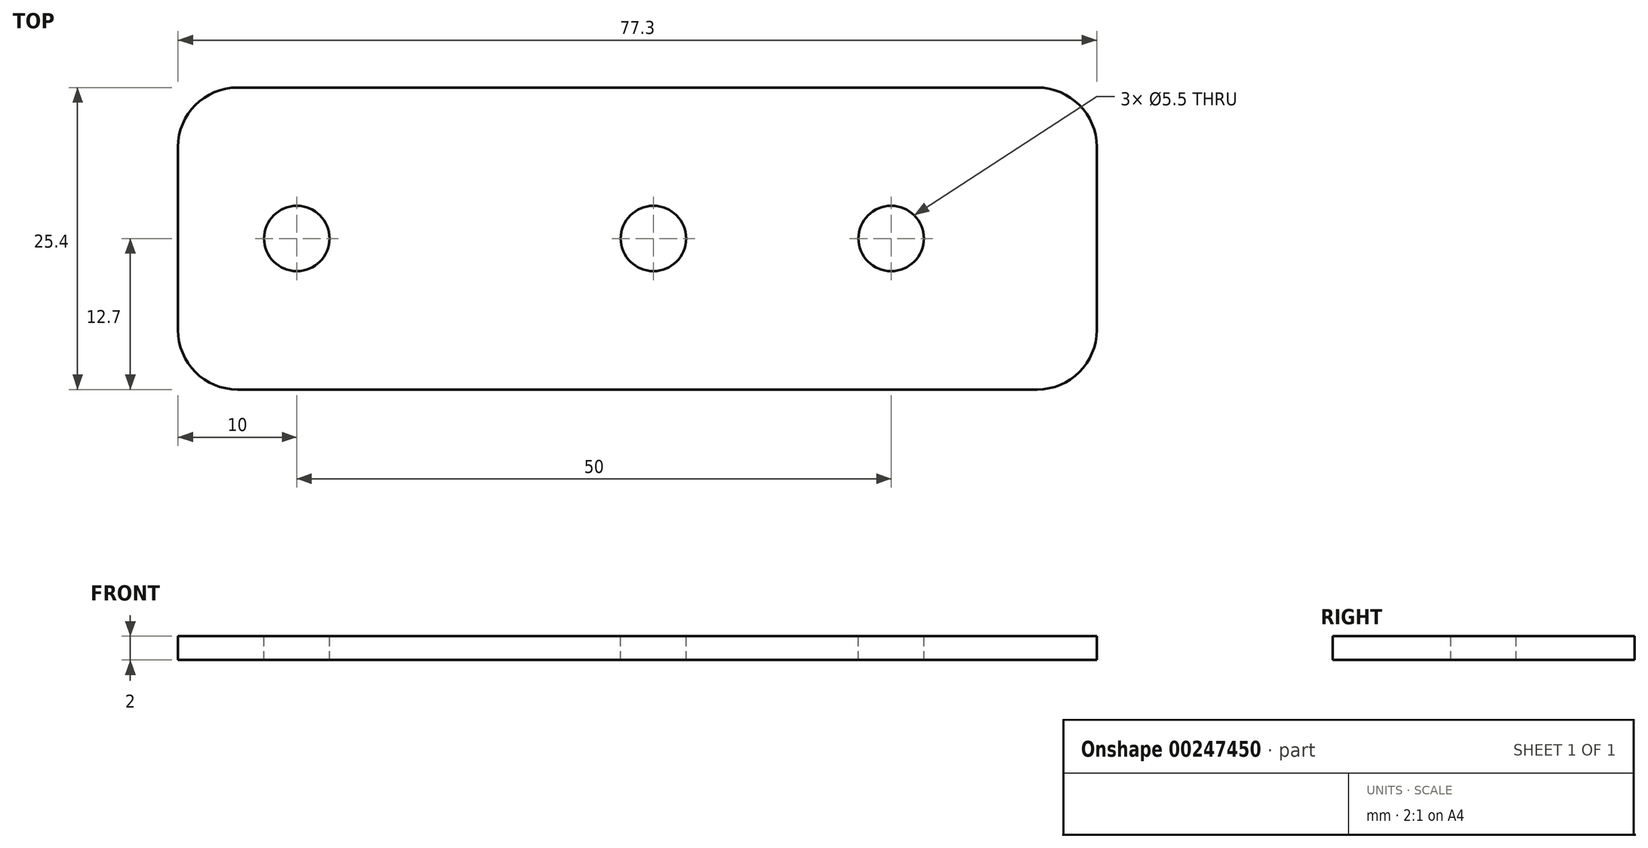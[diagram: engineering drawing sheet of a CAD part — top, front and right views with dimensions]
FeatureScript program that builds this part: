
annotation { "Feature Type Name" : "Feature", "Feature Type Description" : "" }
export const myFeature = defineFeature(function(context is Context, id is Id, definition is map)
    precondition{}
    {
        {
            var Q0;
            Q0=qCreatedBy(makeId("Top.planeOp"),FACE);
            var sketch = newSketch(context, id + "F0", { "sketchPlane" : qUnion([Q0])});
            skLineSegment(sketch, "E0.bottom", {"start": v(0, 0) * mm, "end": v(77.3, 0) * mm});
            skLineSegment(sketch, "E0.top", {"start": v(0, 25.4) * mm, "end": v(77.3, 25.4) * mm});
            skLineSegment(sketch, "E0.left", {"start": v(0, 0) * mm, "end": v(0, 25.4) * mm});
            skLineSegment(sketch, "E0.right", {"start": v(77.3, 0) * mm, "end": v(77.3, 25.4) * mm});
            skSolve(sketch);
        }
        {
            var Q0;
            Q0=makeQuery(id+"F0.imprint","IMPRINT",FACE,{"disambiguationData":[TD([[makeQuery(id+"F0.imprint","IMPRINT",EDGE,{"derivedFrom":sQuery(id+"F0.wireOp",EDGE,"E0.bottom")}),1.0]])]});
            extrude(context, id + "F1", {"entities" : qUnion([Q0]), "depth" : 2 * mm});
        }
        {
            var Q0;
            Q0=makeQuery(id+"F1.opExtrude","CAP_FACE",FACE,{"disambiguationData":[OSD([sQuery(id+"F0.wireOp",EDGE,"E0.bottom"),sQuery(id+"F0.wireOp",EDGE,"E0.top"),sQuery(id+"F0.wireOp",EDGE,"E0.left"),sQuery(id+"F0.wireOp",EDGE,"E0.right")])],"isStart":false});
            var sketch = newSketch(context, id + "F2", { "sketchPlane" : qUnion([Q0])});
            skPoint(sketch, "E1", {"position": v(15.5, 12.7) * mm});
            skLineSegment(sketch, "E2", {"start": v(0, 12.7) * mm, "end": v(77.3, 12.7) * mm});
            skPoint(sketch, "E3", {"position": v(10, 12.7) * mm});
            skPoint(sketch, "E4", {"position": v(60, 12.7) * mm});
            skPoint(sketch, "E5", {"position": v(40, 12.7) * mm});
            skSolve(sketch);
        }
        {
            var Q0;
            Q0=sQuery(id+"F2.wireOp",VERTEX,"E3");
            var Q1;
            Q1=sQuery(id+"F2.wireOp",VERTEX,"E5");
            var Q2;
            Q2=sQuery(id+"F2.wireOp",VERTEX,"E4");
            var Q3;
            Q3=makeQuery(id+"F1.opExtrude","SWEPT_BODY",BODY,{"disambiguationData":[OSD([sQuery(id+"F0.wireOp",EDGE,"E0.bottom"),sQuery(id+"F0.wireOp",EDGE,"E0.top"),sQuery(id+"F0.wireOp",EDGE,"E0.left"),sQuery(id+"F0.wireOp",EDGE,"E0.right")])]});
            hole(context, id + "F3", {"style" : HoleStyle.SIMPLE, "endStyle" : HoleEndStyle.THROUGH, "standardTappedOrClearance" : lookupTablePath({ "standard" : "ISO", "fit" : "Normal", "size" : "M5", "type" : "Clearance" }), "standardBlindInLast" : lookupTablePath({ "fit" : "Standard", "standard" : "ISO", "size" : "M5", "type" : "Clearance" }), "holeDiameter" : 5.5 * mm, "tappedDepth" : 12 * mm, "tapClearance" : 3, "locations" : qUnion([Q0, Q1, Q2]), "scope" : qUnion([Q3])});
        }
        {
            var Q0;
            Q0=makeQuery(id+"F1.opExtrude","SWEPT_EDGE",EDGE,{"disambiguationData":[OSD([sQuery(id+"F0.wireOp",EDGE,"E0.top"),sQuery(id+"F0.wireOp",EDGE,"E0.left")])]});
            var Q1;
            Q1=makeQuery(id+"F1.opExtrude","SWEPT_EDGE",EDGE,{"disambiguationData":[OSD([sQuery(id+"F0.wireOp",EDGE,"E0.bottom"),sQuery(id+"F0.wireOp",EDGE,"E0.left")])]});
            var Q2;
            Q2=makeQuery(id+"F1.opExtrude","SWEPT_EDGE",EDGE,{"disambiguationData":[OSD([sQuery(id+"F0.wireOp",EDGE,"E0.bottom"),sQuery(id+"F0.wireOp",EDGE,"E0.right")])]});
            var Q3;
            Q3=makeQuery(id+"F1.opExtrude","SWEPT_EDGE",EDGE,{"disambiguationData":[OSD([sQuery(id+"F0.wireOp",EDGE,"E0.top"),sQuery(id+"F0.wireOp",EDGE,"E0.right")])]});
            fillet(context, id + "F4", {"entities" : qUnion([Q0, Q1, Q2, Q3]), "radius" : 5 * mm, "tangentPropagation" : true, "allowEdgeOverflow" : false});
        }
    });
